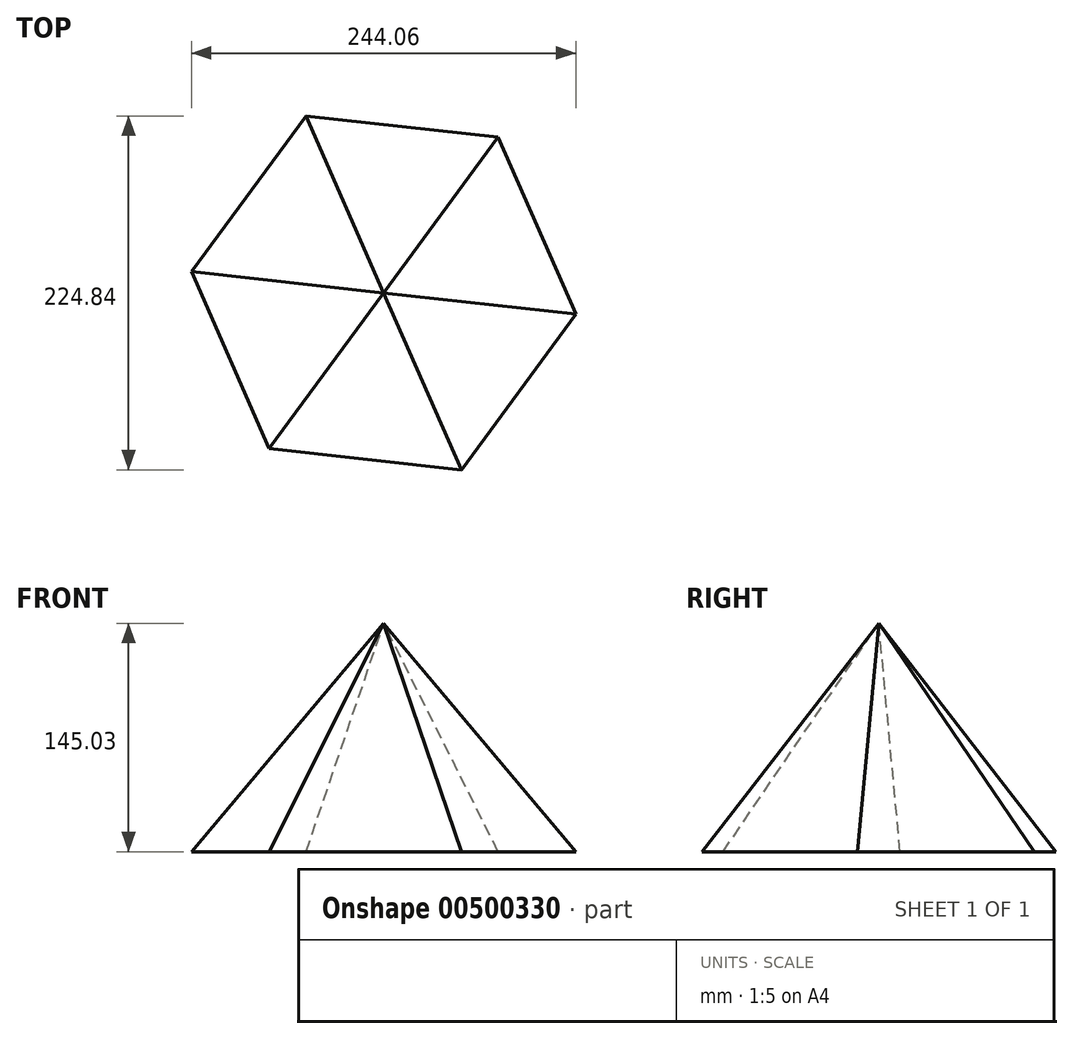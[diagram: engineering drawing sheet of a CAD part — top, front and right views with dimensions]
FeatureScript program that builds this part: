
annotation { "Feature Type Name" : "Feature", "Feature Type Description" : "" }
export const myFeature = defineFeature(function(context is Context, id is Id, definition is map)
    precondition{}
    {
        {
            var Q0;
            Q0=qCreatedBy(makeId("Top.planeOp"),FACE);
            var sketch = newSketch(context, id + "F0", { "sketchPlane" : qUnion([Q0])});
            skCircle(sketch, "E0.cCircle", {"center": v(0, 0) * mm, "radius": 122.77 * mm, "construction": true});
            skLineSegment(sketch, "E0.0", {"start": v(-49.35, 112.42) * mm, "end": v(72.68, 98.95) * mm});
            skLineSegment(sketch, "E0.1", {"start": v(72.68, 98.95) * mm, "end": v(122.03, -13.47) * mm});
            skLineSegment(sketch, "E0.2", {"start": v(122.03, -13.47) * mm, "end": v(49.35, -112.42) * mm});
            skLineSegment(sketch, "E0.3", {"start": v(49.35, -112.42) * mm, "end": v(-72.68, -98.95) * mm});
            skLineSegment(sketch, "E0.4", {"start": v(-72.68, -98.95) * mm, "end": v(-122.03, 13.47) * mm});
            skLineSegment(sketch, "E0.5", {"start": v(-122.03, 13.47) * mm, "end": v(-49.35, 112.42) * mm});
            skSolve(sketch);
        }
        {
            var Q0;
            Q0=qCreatedBy(makeId("Top.planeOp"),FACE);
            cPlane(context, id + "F1", {"entities" : qUnion([Q0]), "cplaneType" : CPlaneType.OFFSET, "offset" : 145.03 * mm, "width" : 152.4 * mm, "height" : 152.4 * mm});
        }
        {
            var Q0;
            Q0=qCreatedBy(id+"F1.planeOp",FACE);
            var sketch = newSketch(context, id + "F2", { "sketchPlane" : qUnion([Q0])});
            skPoint(sketch, "E1", {"position": v(0, 0) * mm});
            skSolve(sketch);
        }
        {
            var Q0;
            Q0=makeQuery(id+"F0.imprint","IMPRINT",FACE,{"disambiguationData":[TD([[makeQuery(id+"F0.imprint","IMPRINT",EDGE,{"derivedFrom":sQuery(id+"F0.wireOp",EDGE,"E0.0")}),-1.0]])]});
            var Q1;
            Q1=sQuery(id+"F2.wireOp",VERTEX,"E1");
            loft(context, id + "F3", {"sheetProfilesArray" : [{ "sheetProfileEntities" : qUnion([Q0]) }, { "sheetProfileEntities" : qUnion([Q1]) }]});
        }
    });
